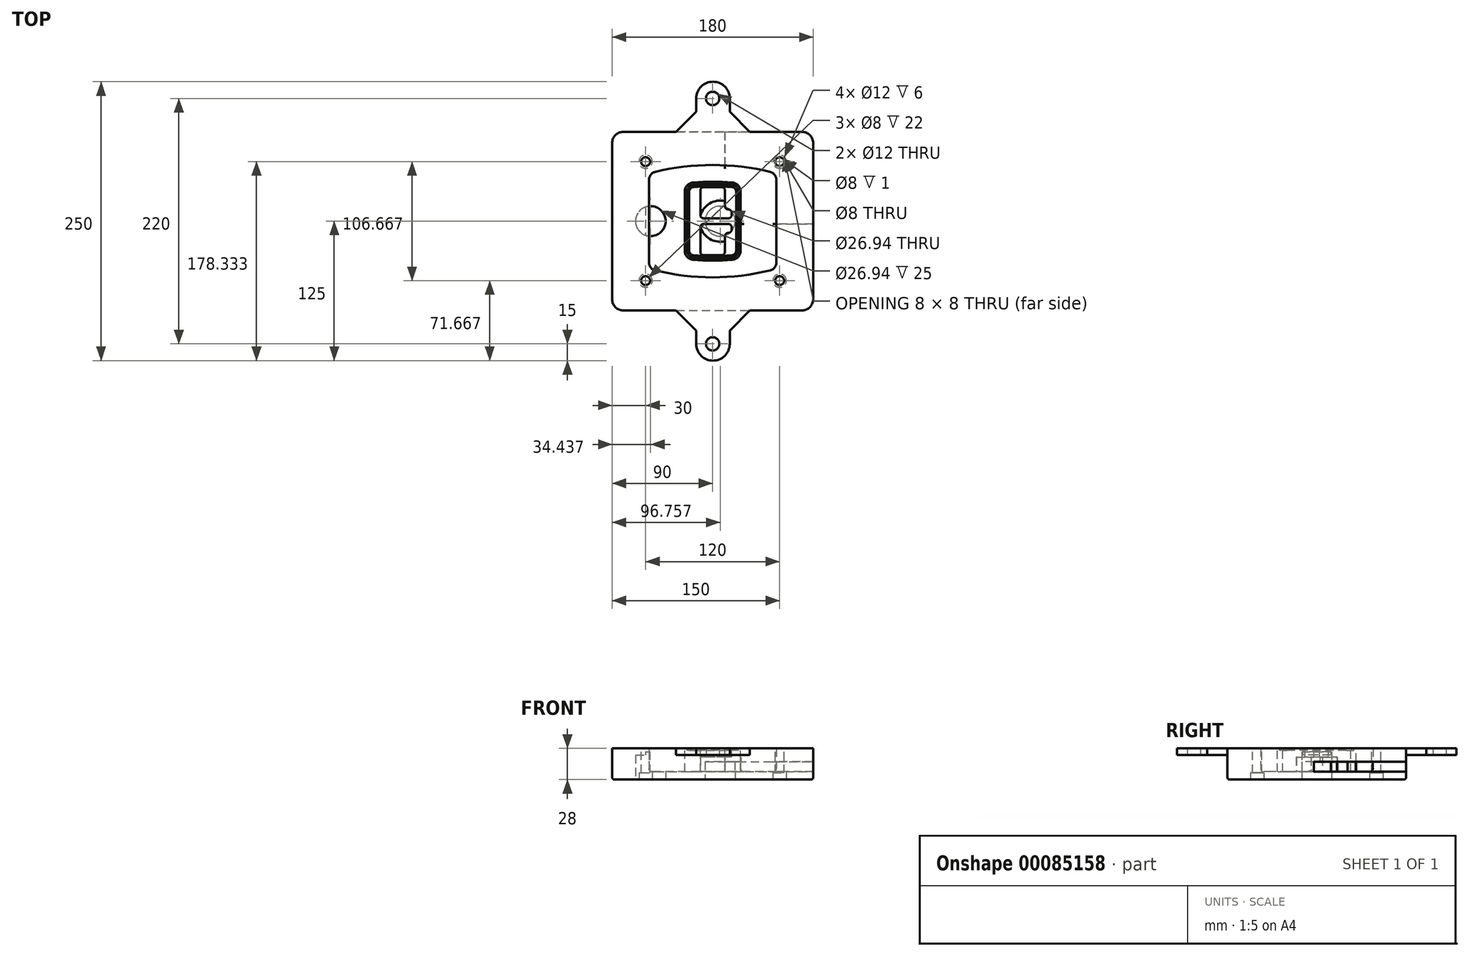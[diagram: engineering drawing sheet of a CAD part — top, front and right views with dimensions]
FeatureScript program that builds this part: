
annotation { "Feature Type Name" : "Feature", "Feature Type Description" : "" }
export const myFeature = defineFeature(function(context is Context, id is Id, definition is map)
    precondition{}
    {
        {
            var Q0;
            Q0=qCreatedBy(makeId("Top.planeOp"),FACE);
            var sketch = newSketch(context, id + "F0", { "sketchPlane" : qUnion([Q0])});
            skPoint(sketch, "E0.rect.middle", {"position": v(0, 0) * mm});
            skLineSegment(sketch, "E1.bottom", {"start": v(-80, -80) * mm, "end": v(80, -80) * mm});
            skLineSegment(sketch, "E1.top", {"start": v(-80, 80) * mm, "end": v(80, 80) * mm});
            skLineSegment(sketch, "E1.left", {"start": v(-90, -70) * mm, "end": v(-90, 70) * mm});
            skLineSegment(sketch, "E1.right", {"start": v(90, -70) * mm, "end": v(90, 70) * mm});
            skLineSegment(sketch, "E2", {"start": v(-90, 80) * mm, "end": v(90, -80) * mm, "construction": true});
            skLineSegment(sketch, "E3", {"start": v(90, 80) * mm, "end": v(-90, -80) * mm, "construction": true});
            skCircle(sketch, "E4", {"center": v(-60, 53.33) * mm, "radius": 4 * mm});
            skCircle(sketch, "E5", {"center": v(60, 53.33) * mm, "radius": 4 * mm});
            skCircle(sketch, "E6", {"center": v(60, -53.33) * mm, "radius": 4 * mm});
            skCircle(sketch, "E7", {"center": v(-60, -53.33) * mm, "radius": 4 * mm});
            skLineSegment(sketch, "E8", {"start": v(-60, 53.33) * mm, "end": v(60, 53.33) * mm, "construction": true});
            skLineSegment(sketch, "E9", {"start": v(60, 53.33) * mm, "end": v(60, -53.33) * mm, "construction": true});
            skLineSegment(sketch, "E10", {"start": v(60, -53.33) * mm, "end": v(-60, -53.33) * mm, "construction": true});
            skLineSegment(sketch, "E11", {"start": v(-60, -53.33) * mm, "end": v(-60, 53.33) * mm, "construction": true});
            skLineSegment(sketch, "E12", {"start": v(-60, 37.3) * mm, "end": v(-60, -37.3) * mm});
            skLineSegment(sketch, "E13", {"start": v(60, 37.3) * mm, "end": v(60, -37.3) * mm});
            skArc(sketch, "E14", {"start": v(52.38, 47.01) * mm, "mid": v(0, 53.33) * mm, "end": v(-52.38, 47.01) * mm});
            skArc(sketch, "E15", {"start": v(-52.38, -47.01) * mm, "mid": v(0, -53.33) * mm, "end": v(52.38, -47.01) * mm});
            skLineSegment(sketch, "E16", {"start": v(-60, 0) * mm, "end": v(60, 0) * mm, "construction": true});
            skPoint(sketch, "E17.visualSharp", {"position": v(-60, -45) * mm});
            skArc(sketch, "E17.filletArc", {"start": v(-60, -37.3) * mm, "mid": v(-57.87, -43.47) * mm, "end": v(-52.38, -47.01) * mm});
            skPoint(sketch, "E18.visualSharp", {"position": v(-60, 45) * mm});
            skArc(sketch, "E18.filletArc", {"start": v(-52.38, 47.01) * mm, "mid": v(-57.87, 43.47) * mm, "end": v(-60, 37.3) * mm});
            skPoint(sketch, "E19.visualSharp", {"position": v(60, 45) * mm});
            skArc(sketch, "E19.filletArc", {"start": v(60, 37.3) * mm, "mid": v(57.87, 43.47) * mm, "end": v(52.38, 47.01) * mm});
            skPoint(sketch, "E20.visualSharp", {"position": v(60, -45) * mm});
            skArc(sketch, "E20.filletArc", {"start": v(52.38, -47.01) * mm, "mid": v(57.87, -43.47) * mm, "end": v(60, -37.3) * mm});
            skPoint(sketch, "E21.visualSharp", {"position": v(-90, 80) * mm});
            skArc(sketch, "E21.filletArc", {"start": v(-80, 80) * mm, "mid": v(-87.07, 77.07) * mm, "end": v(-90, 70) * mm});
            skPoint(sketch, "E22.visualSharp", {"position": v(90, 80) * mm});
            skArc(sketch, "E22.filletArc", {"start": v(90, 70) * mm, "mid": v(87.07, 77.07) * mm, "end": v(80, 80) * mm});
            skPoint(sketch, "E23.visualSharp", {"position": v(90, -80) * mm});
            skArc(sketch, "E23.filletArc", {"start": v(80, -80) * mm, "mid": v(87.07, -77.07) * mm, "end": v(90, -70) * mm});
            skPoint(sketch, "E24.visualSharp", {"position": v(-90, -80) * mm});
            skArc(sketch, "E24.filletArc", {"start": v(-90, -70) * mm, "mid": v(-87.07, -77.07) * mm, "end": v(-80, -80) * mm});
            skArc(sketch, "E25.0", {"start": v(57, 37.3) * mm, "mid": v(55.5, 41.62) * mm, "end": v(51.67, 44.1) * mm});
            skLineSegment(sketch, "E25.1", {"start": v(57, 37.3) * mm, "end": v(57, -37.3) * mm});
            skArc(sketch, "E25.2", {"start": v(51.67, -44.1) * mm, "mid": v(55.5, -41.62) * mm, "end": v(57, -37.3) * mm});
            skArc(sketch, "E25.3", {"start": v(-51.67, -44.1) * mm, "mid": v(0, -50.33) * mm, "end": v(51.67, -44.1) * mm});
            skArc(sketch, "E25.4", {"start": v(-57, -37.3) * mm, "mid": v(-55.5, -41.62) * mm, "end": v(-51.67, -44.1) * mm});
            skArc(sketch, "E25.5", {"start": v(51.67, 44.1) * mm, "mid": v(0, 50.33) * mm, "end": v(-51.67, 44.1) * mm});
            skLineSegment(sketch, "E25.6", {"start": v(-57, 37.3) * mm, "end": v(-57, -37.3) * mm});
            skArc(sketch, "E25.7", {"start": v(-51.67, 44.1) * mm, "mid": v(-55.5, 41.62) * mm, "end": v(-57, 37.3) * mm});
            skArc(sketch, "E26.0", {"start": v(-53.33, 50.9) * mm, "mid": v(-61.01, 45.94) * mm, "end": v(-64, 37.3) * mm});
            skArc(sketch, "E26.1", {"start": v(53.33, 50.9) * mm, "mid": v(0, 57.33) * mm, "end": v(-53.33, 50.9) * mm});
            skArc(sketch, "E26.2", {"start": v(64, 37.3) * mm, "mid": v(61.01, 45.94) * mm, "end": v(53.33, 50.9) * mm});
            skLineSegment(sketch, "E26.3", {"start": v(64, 37.3) * mm, "end": v(64, -37.3) * mm});
            skArc(sketch, "E26.4", {"start": v(53.33, -50.9) * mm, "mid": v(61.01, -45.94) * mm, "end": v(64, -37.3) * mm});
            skLineSegment(sketch, "E26.5", {"start": v(-64, 37.3) * mm, "end": v(-64, -37.3) * mm});
            skArc(sketch, "E26.6", {"start": v(-53.33, -50.9) * mm, "mid": v(0, -57.33) * mm, "end": v(53.33, -50.9) * mm});
            skArc(sketch, "E26.7", {"start": v(-64, -37.3) * mm, "mid": v(-61.01, -45.94) * mm, "end": v(-53.33, -50.9) * mm});
            skSolve(sketch);
        }
        {
            var Q0;
            Q0=makeQuery(id+"F0.imprint","IMPRINT",FACE,{"disambiguationData":[TD([[makeQuery(id+"F0.imprint","IMPRINT",EDGE,{"derivedFrom":sQuery(id+"F0.wireOp",EDGE,"E1.bottom")}),1.0]])]});
            var Q1;
            Q1=makeQuery(id+"F0.imprint","IMPRINT",FACE,{"disambiguationData":[TD([[makeQuery(id+"F0.imprint","IMPRINT",EDGE,{"derivedFrom":sQuery(id+"F0.wireOp",EDGE,"E12")}),1.0]])]});
            var Q2;
            Q2=makeQuery(id+"F0.imprint","IMPRINT",FACE,{"disambiguationData":[TD([[makeQuery(id+"F0.imprint","IMPRINT",EDGE,{"derivedFrom":sQuery(id+"F0.wireOp",EDGE,"E25.0")}),1.0]])]});
            var Q3;
            Q3=makeQuery(id+"F0.imprint","IMPRINT",FACE,{"disambiguationData":[TD([[makeQuery(id+"F0.imprint","IMPRINT",EDGE,{"derivedFrom":sQuery(id+"F0.wireOp",EDGE,"E12")}),-1.0]])]});
            extrude(context, id + "F1", {"entities" : qUnion([Q0, Q1, Q2, Q3]), "oppositeDirection" : true, "depth" : 25 * mm});
        }
        {
            var Q0;
            Q0=makeQuery(id+"F0.imprint","IMPRINT",FACE,{"disambiguationData":[TD([[makeQuery(id+"F0.imprint","IMPRINT",EDGE,{"derivedFrom":sQuery(id+"F0.wireOp",EDGE,"E12")}),1.0]])]});
            extrude(context, id + "F2", {"entities" : qUnion([Q0]), "operationType" : NewBodyOperationType.ADD, "depth" : 3 * mm});
        }
        {
            var Q0;
            Q0=makeQuery(id+"F0.imprint","IMPRINT",FACE,{"disambiguationData":[TD([[makeQuery(id+"F0.imprint","IMPRINT",EDGE,{"derivedFrom":sQuery(id+"F0.wireOp",EDGE,"E25.0")}),1.0]])]});
            extrude(context, id + "F3", {"entities" : qUnion([Q0]), "operationType" : NewBodyOperationType.REMOVE, "oppositeDirection" : true, "depth" : 18 * mm});
        }
        {
            var Q0;
            Q0=makeQuery(id+"F2.opExtrude","CAP_FACE",FACE,{"disambiguationData":[OSD([sQuery(id+"F0.wireOp",EDGE,"E12"),sQuery(id+"F0.wireOp",EDGE,"E13"),sQuery(id+"F0.wireOp",EDGE,"E14"),sQuery(id+"F0.wireOp",EDGE,"E15"),sQuery(id+"F0.wireOp",EDGE,"E17.filletArc"),sQuery(id+"F0.wireOp",EDGE,"E18.filletArc"),sQuery(id+"F0.wireOp",EDGE,"E19.filletArc"),sQuery(id+"F0.wireOp",EDGE,"E20.filletArc"),sQuery(id+"F0.wireOp",EDGE,"E25.0"),sQuery(id+"F0.wireOp",EDGE,"E25.1"),sQuery(id+"F0.wireOp",EDGE,"E25.2"),sQuery(id+"F0.wireOp",EDGE,"E25.3"),sQuery(id+"F0.wireOp",EDGE,"E25.4"),sQuery(id+"F0.wireOp",EDGE,"E25.5"),sQuery(id+"F0.wireOp",EDGE,"E25.6"),sQuery(id+"F0.wireOp",EDGE,"E25.7")])],"isStart":false});
            var sketch = newSketch(context, id + "F4", { "sketchPlane" : qUnion([Q0])});
            skArc(sketch, "E27.0", {"start": v(-17.7, -34.56) * mm, "mid": v(0, -35.33) * mm, "end": v(17.7, -34.56) * mm});
            skArc(sketch, "E28.0", {"start": v(17.7, 34.56) * mm, "mid": v(0, 35.33) * mm, "end": v(-17.7, 34.56) * mm});
            skLineSegment(sketch, "E29", {"start": v(-25, 26.59) * mm, "end": v(-25, -26.59) * mm});
            skLineSegment(sketch, "E30", {"start": v(25, 26.59) * mm, "end": v(25, -26.59) * mm});
            skLineSegment(sketch, "E31", {"start": v(-25, 33.78) * mm, "end": v(25, 33.78) * mm, "construction": true});
            skLineSegment(sketch, "E32", {"start": v(-25, -33.78) * mm, "end": v(25, -33.78) * mm, "construction": true});
            skPoint(sketch, "E33.visualSharp", {"position": v(-25, 33.78) * mm});
            skArc(sketch, "E33.filletArc", {"start": v(-17.7, 34.56) * mm, "mid": v(-22.9, 32) * mm, "end": v(-25, 26.59) * mm});
            skPoint(sketch, "E34.visualSharp", {"position": v(25, 33.78) * mm});
            skArc(sketch, "E34.filletArc", {"start": v(25, 26.59) * mm, "mid": v(22.9, 32) * mm, "end": v(17.7, 34.56) * mm});
            skPoint(sketch, "E35.visualSharp", {"position": v(25, -33.78) * mm});
            skArc(sketch, "E35.filletArc", {"start": v(17.7, -34.56) * mm, "mid": v(22.9, -32) * mm, "end": v(25, -26.59) * mm});
            skPoint(sketch, "E36.visualSharp", {"position": v(-25, -33.78) * mm});
            skArc(sketch, "E36.filletArc", {"start": v(-25, -26.59) * mm, "mid": v(-22.9, -32) * mm, "end": v(-17.7, -34.56) * mm});
            skArc(sketch, "E37.0", {"start": v(51.67, 44.1) * mm, "mid": v(0, 50.33) * mm, "end": v(-51.67, 44.1) * mm});
            skArc(sketch, "E37.1", {"start": v(-51.67, 44.1) * mm, "mid": v(-55.5, 41.62) * mm, "end": v(-57, 37.3) * mm});
            skLineSegment(sketch, "E37.2", {"start": v(-57, 37.3) * mm, "end": v(-57, -37.3) * mm});
            skArc(sketch, "E37.3", {"start": v(-57, -37.3) * mm, "mid": v(-55.5, -41.62) * mm, "end": v(-51.67, -44.1) * mm});
            skArc(sketch, "E37.4", {"start": v(-51.67, -44.1) * mm, "mid": v(0, -50.33) * mm, "end": v(51.67, -44.1) * mm});
            skArc(sketch, "E37.5", {"start": v(51.67, -44.1) * mm, "mid": v(55.5, -41.62) * mm, "end": v(57, -37.3) * mm});
            skLineSegment(sketch, "E37.6", {"start": v(57, 37.3) * mm, "end": v(57, -37.3) * mm});
            skArc(sketch, "E37.7", {"start": v(57, 37.3) * mm, "mid": v(55.5, 41.62) * mm, "end": v(51.67, 44.1) * mm});
            skLineSegment(sketch, "E38.0", {"start": v(23, 26.59) * mm, "end": v(23, -26.59) * mm});
            skArc(sketch, "E38.1", {"start": v(17.53, -32.56) * mm, "mid": v(21.42, -30.64) * mm, "end": v(23, -26.59) * mm});
            skArc(sketch, "E38.2", {"start": v(-17.53, -32.56) * mm, "mid": v(0, -33.33) * mm, "end": v(17.53, -32.56) * mm});
            skArc(sketch, "E38.3", {"start": v(-23, -26.59) * mm, "mid": v(-21.42, -30.64) * mm, "end": v(-17.53, -32.56) * mm});
            skLineSegment(sketch, "E38.4", {"start": v(-23, 26.59) * mm, "end": v(-23, -26.59) * mm});
            skArc(sketch, "E38.5", {"start": v(23, 26.59) * mm, "mid": v(21.42, 30.64) * mm, "end": v(17.53, 32.56) * mm});
            skArc(sketch, "E38.6", {"start": v(-17.53, 32.56) * mm, "mid": v(-21.42, 30.64) * mm, "end": v(-23, 26.59) * mm});
            skArc(sketch, "E38.7", {"start": v(17.53, 32.56) * mm, "mid": v(0, 33.33) * mm, "end": v(-17.53, 32.56) * mm});
            skArc(sketch, "E39.0", {"start": v(21, 26.59) * mm, "mid": v(19.95, 29.29) * mm, "end": v(17.35, 30.57) * mm});
            skLineSegment(sketch, "E39.1", {"start": v(21, 26.59) * mm, "end": v(21, -26.59) * mm});
            skArc(sketch, "E39.2", {"start": v(17.35, -30.57) * mm, "mid": v(19.95, -29.29) * mm, "end": v(21, -26.59) * mm});
            skArc(sketch, "E39.3", {"start": v(-17.35, -30.57) * mm, "mid": v(0, -31.33) * mm, "end": v(17.35, -30.57) * mm});
            skArc(sketch, "E39.4", {"start": v(-21, -26.59) * mm, "mid": v(-19.95, -29.29) * mm, "end": v(-17.35, -30.57) * mm});
            skArc(sketch, "E39.5", {"start": v(17.35, 30.57) * mm, "mid": v(0, 31.33) * mm, "end": v(-17.35, 30.57) * mm});
            skLineSegment(sketch, "E39.6", {"start": v(-21, 26.59) * mm, "end": v(-21, -26.59) * mm});
            skArc(sketch, "E39.7", {"start": v(-17.35, 30.57) * mm, "mid": v(-19.95, 29.29) * mm, "end": v(-21, 26.59) * mm});
            skLineSegment(sketch, "E40", {"start": v(-25, 0) * mm, "end": v(25, 0) * mm, "construction": true});
            skLineSegment(sketch, "E41", {"start": v(-11, 5.5) * mm, "end": v(-11, 27.5) * mm});
            skLineSegment(sketch, "E42", {"start": v(-8, 30.5) * mm, "end": v(8, 30.5) * mm});
            skLineSegment(sketch, "E43", {"start": v(11, 27.5) * mm, "end": v(11, 13.5) * mm});
            skLineSegment(sketch, "E44", {"start": v(14, 10.5) * mm, "end": v(14, 10.5) * mm});
            skLineSegment(sketch, "E45", {"start": v(17, 7.5) * mm, "end": v(17, 5.5) * mm});
            skLineSegment(sketch, "E46", {"start": v(14, 2.5) * mm, "end": v(-8, 2.5) * mm});
            skPoint(sketch, "E47.visualSharp", {"position": v(-11, 30.5) * mm});
            skArc(sketch, "E47.filletArc", {"start": v(-8, 30.5) * mm, "mid": v(-10.12, 29.62) * mm, "end": v(-11, 27.5) * mm});
            skPoint(sketch, "E48.visualSharp", {"position": v(11, 30.5) * mm});
            skArc(sketch, "E48.filletArc", {"start": v(11, 27.5) * mm, "mid": v(10.12, 29.62) * mm, "end": v(8, 30.5) * mm});
            skPoint(sketch, "E49.visualSharp", {"position": v(11, 10.5) * mm});
            skArc(sketch, "E49.filletArc", {"start": v(11, 13.5) * mm, "mid": v(11.88, 11.38) * mm, "end": v(14, 10.5) * mm});
            skPoint(sketch, "E50.visualSharp", {"position": v(17, 10.5) * mm});
            skArc(sketch, "E50.filletArc", {"start": v(17, 7.5) * mm, "mid": v(16.12, 9.62) * mm, "end": v(14, 10.5) * mm});
            skPoint(sketch, "E51.visualSharp", {"position": v(17, 2.5) * mm});
            skArc(sketch, "E51.filletArc", {"start": v(14, 2.5) * mm, "mid": v(16.12, 3.38) * mm, "end": v(17, 5.5) * mm});
            skPoint(sketch, "E52.visualSharp", {"position": v(-11, 2.5) * mm});
            skArc(sketch, "E52.filletArc", {"start": v(-11, 5.5) * mm, "mid": v(-10.12, 3.38) * mm, "end": v(-8, 2.5) * mm});
            skLineSegment(sketch, "E53.0.MirrorCS", {"start": v(14, -2.5) * mm, "end": v(-8, -2.5) * mm});
            skArc(sketch, "E54.0.MirrorCS", {"start": v(-11, -5.5) * mm, "mid": v(-10.12, -3.38) * mm, "end": v(-8, -2.5) * mm});
            skLineSegment(sketch, "E55.0.MirrorCS", {"start": v(-11, -5.5) * mm, "end": v(-11, -27.5) * mm});
            skArc(sketch, "E56.0.MirrorCS", {"start": v(-8, -30.5) * mm, "mid": v(-10.12, -29.62) * mm, "end": v(-11, -27.5) * mm});
            skLineSegment(sketch, "E57.0.MirrorCS", {"start": v(-8, -30.5) * mm, "end": v(8, -30.5) * mm});
            skArc(sketch, "E58.0.MirrorCS", {"start": v(11, -27.5) * mm, "mid": v(10.12, -29.62) * mm, "end": v(8, -30.5) * mm});
            skLineSegment(sketch, "E59.0.MirrorCS", {"start": v(11, -27.5) * mm, "end": v(11, -13.5) * mm});
            skArc(sketch, "E60.0.MirrorCS", {"start": v(11, -13.5) * mm, "mid": v(11.88, -11.38) * mm, "end": v(14, -10.5) * mm});
            skArc(sketch, "E61.0.MirrorCS", {"start": v(17, -7.5) * mm, "mid": v(16.12, -9.62) * mm, "end": v(14, -10.5) * mm});
            skLineSegment(sketch, "E62.0.MirrorCS", {"start": v(17, -7.5) * mm, "end": v(17, -5.5) * mm});
            skArc(sketch, "E63.0.MirrorCS", {"start": v(14, -2.5) * mm, "mid": v(16.12, -3.38) * mm, "end": v(17, -5.5) * mm});
            skSolve(sketch);
        }
        {
            var Q0;
            Q0=makeQuery(id+"F4.imprint","IMPRINT",FACE,{"disambiguationData":[TD([[makeQuery(id+"F4.imprint","IMPRINT",EDGE,{"derivedFrom":sQuery(id+"F4.wireOp",EDGE,"E27.0")}),1.0]])]});
            var Q1;
            Q1=makeQuery(id+"F4.imprint","IMPRINT",FACE,{"disambiguationData":[TD([[makeQuery(id+"F4.imprint","IMPRINT",EDGE,{"derivedFrom":sQuery(id+"F4.wireOp",EDGE,"E38.0")}),-1.0]])]});
            var Q2;
            Q2=makeQuery(id+"F4.imprint","IMPRINT",FACE,{"disambiguationData":[TD([[makeQuery(id+"F4.imprint","IMPRINT",EDGE,{"derivedFrom":sQuery(id+"F4.wireOp",EDGE,"E39.0")}),1.0]])]});
            extrude(context, id + "F5", {"entities" : qUnion([Q0, Q1, Q2]), "operationType" : NewBodyOperationType.ADD, "endBound" : BoundingType.UP_TO_NEXT, "oppositeDirection" : true, "depth" : 25 * mm});
        }
        {
            var Q0;
            Q0=makeQuery(id+"F4.imprint","IMPRINT",FACE,{"disambiguationData":[TD([[makeQuery(id+"F4.imprint","IMPRINT",EDGE,{"derivedFrom":sQuery(id+"F4.wireOp",EDGE,"E38.0")}),-1.0]])]});
            extrude(context, id + "F6", {"entities" : qUnion([Q0]), "operationType" : NewBodyOperationType.REMOVE, "oppositeDirection" : true, "depth" : 2 * mm});
        }
        {
            var Q0;
            Q0=makeQuery(id+"F1.opExtrude","CAP_FACE",FACE,{"disambiguationData":[OSD([sQuery(id+"F0.wireOp",EDGE,"E1.bottom"),sQuery(id+"F0.wireOp",EDGE,"E1.top"),sQuery(id+"F0.wireOp",EDGE,"E1.left"),sQuery(id+"F0.wireOp",EDGE,"E1.right"),sQuery(id+"F0.wireOp",EDGE,"E4"),sQuery(id+"F0.wireOp",EDGE,"E5"),sQuery(id+"F0.wireOp",EDGE,"E6"),sQuery(id+"F0.wireOp",EDGE,"E7"),sQuery(id+"F0.wireOp",EDGE,"E21.filletArc"),sQuery(id+"F0.wireOp",EDGE,"E22.filletArc"),sQuery(id+"F0.wireOp",EDGE,"E23.filletArc"),sQuery(id+"F0.wireOp",EDGE,"E24.filletArc")])],"isStart":false});
            var sketch = newSketch(context, id + "F7", { "sketchPlane" : qUnion([Q0])});
            skCircle(sketch, "E64", {"center": v(6.76, 0) * mm, "radius": 13.47 * mm});
            skCircle(sketch, "E65", {"center": v(-55.56, 0) * mm, "radius": 13.47 * mm});
            skLineSegment(sketch, "E66", {"start": v(90, 0) * mm, "end": v(-90, 0) * mm});
            skCircle(sketch, "E67", {"center": v(6.76, 0) * mm, "radius": 18.47 * mm});
            skCircle(sketch, "E68", {"center": v(60, -53.33) * mm, "radius": 6 * mm});
            skCircle(sketch, "E69", {"center": v(-60, -53.33) * mm, "radius": 6 * mm});
            skCircle(sketch, "E70", {"center": v(-60, 53.33) * mm, "radius": 6 * mm});
            skCircle(sketch, "E71", {"center": v(60, 53.33) * mm, "radius": 6 * mm});
            skSolve(sketch);
        }
        {
            var Q0;
            {var subQ1=sQuery(id+"F7.wireOp",EDGE,"E66");var subQ4=sQuery(id+"F7.wireOp",EDGE,"E64");var subQ6=makeQuery(id+"F7.imprint","INTERSECT",VERTEX,{"disambiguationData":[OD(0.0)],"derivedFrom":[subQ4,subQ1]});Q0=makeQuery(id+"F7.imprint","IMPRINT",FACE,{"disambiguationData":[TD([[makeQuery(id+"F7.imprint","IMPRINT",EDGE,{"disambiguationData":[TD([[subQ6,-1.0]])],"derivedFrom":subQ4}),-1.0]])]});}
            var Q1;
            {var subQ0=sQuery(id+"F7.wireOp",EDGE,"E66");var subQ1=sQuery(id+"F7.wireOp",EDGE,"E64");var subQ3=makeQuery(id+"F7.imprint","INTERSECT",VERTEX,{"disambiguationData":[OD(0.0)],"derivedFrom":[subQ1,subQ0]});Q1=makeQuery(id+"F7.imprint","IMPRINT",FACE,{"disambiguationData":[TD([[makeQuery(id+"F7.imprint","IMPRINT",EDGE,{"disambiguationData":[TD([[subQ3,-1.0]])],"derivedFrom":subQ1}),1.0]])]});}
            var Q2;
            {var subQ0=sQuery(id+"F7.wireOp",EDGE,"E66");var subQ1=sQuery(id+"F7.wireOp",EDGE,"E64");var subQ3=makeQuery(id+"F7.imprint","INTERSECT",VERTEX,{"disambiguationData":[OD(0.0)],"derivedFrom":[subQ1,subQ0]});Q2=makeQuery(id+"F7.imprint","IMPRINT",FACE,{"disambiguationData":[TD([[makeQuery(id+"F7.imprint","IMPRINT",EDGE,{"disambiguationData":[TD([[subQ3,1.0]])],"derivedFrom":subQ1}),1.0]])]});}
            var Q3;
            {var subQ1=sQuery(id+"F7.wireOp",EDGE,"E66");var subQ4=sQuery(id+"F7.wireOp",EDGE,"E64");var subQ6=makeQuery(id+"F7.imprint","INTERSECT",VERTEX,{"disambiguationData":[OD(0.0)],"derivedFrom":[subQ4,subQ1]});Q3=makeQuery(id+"F7.imprint","IMPRINT",FACE,{"disambiguationData":[TD([[makeQuery(id+"F7.imprint","IMPRINT",EDGE,{"disambiguationData":[TD([[subQ6,1.0]])],"derivedFrom":subQ4}),-1.0]])]});}
            extrude(context, id + "F8", {"entities" : qUnion([Q0, Q1, Q2, Q3]), "operationType" : NewBodyOperationType.ADD, "oppositeDirection" : true, "depth" : 20 * mm});
        }
        {
            var Q0;
            {var subQ0=sQuery(id+"F7.wireOp",EDGE,"E66");var subQ1=sQuery(id+"F7.wireOp",EDGE,"E64");var subQ3=makeQuery(id+"F7.imprint","INTERSECT",VERTEX,{"disambiguationData":[OD(0.0)],"derivedFrom":[subQ1,subQ0]});Q0=makeQuery(id+"F7.imprint","IMPRINT",FACE,{"disambiguationData":[TD([[makeQuery(id+"F7.imprint","IMPRINT",EDGE,{"disambiguationData":[TD([[subQ3,-1.0]])],"derivedFrom":subQ1}),1.0]])]});}
            var Q1;
            {var subQ0=sQuery(id+"F7.wireOp",EDGE,"E66");var subQ1=sQuery(id+"F7.wireOp",EDGE,"E64");var subQ3=makeQuery(id+"F7.imprint","INTERSECT",VERTEX,{"disambiguationData":[OD(0.0)],"derivedFrom":[subQ1,subQ0]});Q1=makeQuery(id+"F7.imprint","IMPRINT",FACE,{"disambiguationData":[TD([[makeQuery(id+"F7.imprint","IMPRINT",EDGE,{"disambiguationData":[TD([[subQ3,1.0]])],"derivedFrom":subQ1}),1.0]])]});}
            extrude(context, id + "F9", {"entities" : qUnion([Q0, Q1]), "operationType" : NewBodyOperationType.REMOVE, "oppositeDirection" : true, "depth" : 16 * mm});
        }
        {
            var Q0;
            {var subQ0=sQuery(id+"F7.wireOp",EDGE,"E66");var subQ1=sQuery(id+"F7.wireOp",EDGE,"E65");var subQ3=makeQuery(id+"F7.imprint","INTERSECT",VERTEX,{"disambiguationData":[OD(0.0)],"derivedFrom":[subQ1,subQ0]});Q0=makeQuery(id+"F7.imprint","IMPRINT",FACE,{"disambiguationData":[TD([[makeQuery(id+"F7.imprint","IMPRINT",EDGE,{"disambiguationData":[TD([[subQ3,-1.0]])],"derivedFrom":subQ1}),1.0]])]});}
            var Q1;
            {var subQ0=sQuery(id+"F7.wireOp",EDGE,"E66");var subQ1=sQuery(id+"F7.wireOp",EDGE,"E65");var subQ3=makeQuery(id+"F7.imprint","INTERSECT",VERTEX,{"disambiguationData":[OD(0.0)],"derivedFrom":[subQ1,subQ0]});Q1=makeQuery(id+"F7.imprint","IMPRINT",FACE,{"disambiguationData":[TD([[makeQuery(id+"F7.imprint","IMPRINT",EDGE,{"disambiguationData":[TD([[subQ3,1.0]])],"derivedFrom":subQ1}),1.0]])]});}
            extrude(context, id + "F10", {"entities" : qUnion([Q0, Q1]), "operationType" : NewBodyOperationType.REMOVE, "oppositeDirection" : true, "depth" : 25 * mm});
        }
        {
            var Q0;
            Q0=makeQuery(id+"F7.imprint","IMPRINT",FACE,{"disambiguationData":[TD([[makeQuery(id+"F7.imprint","IMPRINT",EDGE,{"derivedFrom":sQuery(id+"F7.wireOp",EDGE,"E68")}),1.0]])]});
            var Q1;
            Q1=makeQuery(id+"F7.imprint","IMPRINT",FACE,{"disambiguationData":[TD([[makeQuery(id+"F7.imprint","IMPRINT",EDGE,{"derivedFrom":makeQuery(id+"F1.opExtrude","CAP_EDGE",EDGE,{"disambiguationData":[OSD([sQuery(id+"F0.wireOp",EDGE,"E5")])],"isStart":false})}),-1.0]])]});
            var Q2;
            Q2=makeQuery(id+"F7.imprint","IMPRINT",FACE,{"disambiguationData":[TD([[makeQuery(id+"F7.imprint","IMPRINT",EDGE,{"derivedFrom":sQuery(id+"F7.wireOp",EDGE,"E69")}),1.0]])]});
            var Q3;
            Q3=makeQuery(id+"F7.imprint","IMPRINT",FACE,{"disambiguationData":[TD([[makeQuery(id+"F7.imprint","IMPRINT",EDGE,{"derivedFrom":makeQuery(id+"F1.opExtrude","CAP_EDGE",EDGE,{"disambiguationData":[OSD([sQuery(id+"F0.wireOp",EDGE,"E4")])],"isStart":false})}),-1.0]])]});
            var Q4;
            Q4=makeQuery(id+"F7.imprint","IMPRINT",FACE,{"disambiguationData":[TD([[makeQuery(id+"F7.imprint","IMPRINT",EDGE,{"derivedFrom":sQuery(id+"F7.wireOp",EDGE,"E70")}),1.0]])]});
            var Q5;
            Q5=makeQuery(id+"F7.imprint","IMPRINT",FACE,{"disambiguationData":[TD([[makeQuery(id+"F7.imprint","IMPRINT",EDGE,{"derivedFrom":makeQuery(id+"F1.opExtrude","CAP_EDGE",EDGE,{"disambiguationData":[OSD([sQuery(id+"F0.wireOp",EDGE,"E7")])],"isStart":false})}),-1.0]])]});
            var Q6;
            Q6=makeQuery(id+"F7.imprint","IMPRINT",FACE,{"disambiguationData":[TD([[makeQuery(id+"F7.imprint","IMPRINT",EDGE,{"derivedFrom":sQuery(id+"F7.wireOp",EDGE,"E71")}),1.0]])]});
            var Q7;
            Q7=makeQuery(id+"F7.imprint","IMPRINT",FACE,{"disambiguationData":[TD([[makeQuery(id+"F7.imprint","IMPRINT",EDGE,{"derivedFrom":makeQuery(id+"F1.opExtrude","CAP_EDGE",EDGE,{"disambiguationData":[OSD([sQuery(id+"F0.wireOp",EDGE,"E6")])],"isStart":false})}),-1.0]])]});
            extrude(context, id + "F11", {"entities" : qUnion([Q0, Q1, Q2, Q3, Q4, Q5, Q6, Q7]), "operationType" : NewBodyOperationType.REMOVE, "oppositeDirection" : true, "depth" : 6 * mm});
        }
        {
            var Q0;
            Q0=makeQuery(id+"F9.boolean.opBoolean","COPY",FACE,{"derivedFrom":makeQuery(id+"F9.opExtrude","CAP_FACE",FACE,{"disambiguationData":[OSD([sQuery(id+"F7.wireOp",EDGE,"E64")])],"isStart":false})});
            var sketch = newSketch(context, id + "F12", { "sketchPlane" : qUnion([Q0])});
            skArc(sketch, "E72.0", {"start": v(11, -88.19) * mm, "mid": v(97.1, -83.6) * mm, "end": v(92.5, 2.5) * mm});
            skLineSegment(sketch, "E72.1", {"start": v(11, -17.97) * mm, "end": v(11, -17.97) * mm});
            skLineSegment(sketch, "E73", {"start": v(92.5, -105.13) * mm, "end": v(102.3, -105.13) * mm});
            skLineSegment(sketch, "E74.0", {"start": v(92.5, 2.5) * mm, "end": v(14, 2.5) * mm});
            skArc(sketch, "E74.1", {"start": v(14, 2.5) * mm, "mid": v(16.12, 3.38) * mm, "end": v(17, 5.5) * mm});
            skLineSegment(sketch, "E74.2", {"start": v(17, 7.5) * mm, "end": v(17, 5.5) * mm});
            skArc(sketch, "E74.3", {"start": v(17, 7.5) * mm, "mid": v(16.12, 9.62) * mm, "end": v(14, 10.5) * mm});
            skArc(sketch, "E74.4", {"start": v(11, 13.5) * mm, "mid": v(11.88, 11.38) * mm, "end": v(14, 10.5) * mm});
            skLineSegment(sketch, "E74.5", {"start": v(11, 13.5) * mm, "end": v(11, -88.19) * mm});
            skLineSegment(sketch, "E74.7", {"start": v(92.5, -2.5) * mm, "end": v(14, -2.5) * mm});
            skArc(sketch, "E74.8", {"start": v(14, -2.5) * mm, "mid": v(16.12, -3.38) * mm, "end": v(17, -5.5) * mm});
            skLineSegment(sketch, "E74.9", {"start": v(17, -7.5) * mm, "end": v(17, -5.5) * mm});
            skArc(sketch, "E74.10", {"start": v(17, -7.5) * mm, "mid": v(16.12, -9.62) * mm, "end": v(14, -10.5) * mm});
            skArc(sketch, "E74.11", {"start": v(11, -13.5) * mm, "mid": v(11.88, -11.38) * mm, "end": v(14, -10.5) * mm});
            skLineSegment(sketch, "E74.12", {"start": v(11, -17.97) * mm, "end": v(11, -13.5) * mm});
            skPoint(sketch, "E75.orphan", {"position": v(11, -27.5) * mm});
            skPoint(sketch, "E76.orphan", {"position": v(-8, -2.5) * mm});
            skPoint(sketch, "E77.orphan", {"position": v(-8, 2.5) * mm});
            skPoint(sketch, "E78.orphan", {"position": v(11, 27.5) * mm});
            skSolve(sketch);
        }
        {
            var Q0;
            {var subQ7=sQuery(id+"F12.wireOp",EDGE,"E72.0");var subQ14=sQuery(id+"F12.wireOp",EDGE,"E72.1");var subQ16=sQuery(id+"F12.wireOp",EDGE,"E74.1");var subQ18=sQuery(id+"F12.wireOp",EDGE,"E74.8");Q0=qUnion([makeQuery(id+"F12.imprint","IMPRINT",FACE,{"disambiguationData":[TD([[makeQuery(id+"F12.imprint","IMPRINT",EDGE,{"derivedFrom":subQ7}),1.0]])]}),makeQuery(id+"F12.imprint","IMPRINT",FACE,{"disambiguationData":[TD([[makeQuery(id+"F12.imprint","IMPRINT",EDGE,{"derivedFrom":subQ14}),1.0]])]}),makeQuery(id+"F12.imprint","IMPRINT",FACE,{"disambiguationData":[TD([[makeQuery(id+"F12.imprint","IMPRINT",EDGE,{"derivedFrom":subQ16}),1.0]])]}),makeQuery(id+"F12.imprint","IMPRINT",FACE,{"disambiguationData":[TD([[makeQuery(id+"F12.imprint","IMPRINT",EDGE,{"derivedFrom":subQ18}),-1.0]])]})]);}
            var Q1;
            Q1=makeQuery(id+"F5.boolean.opBoolean","SPLIT",FACE,{"disambiguationData":[TD([makeQuery(id+"F5.opExtrude","SWEPT_FACE",FACE,{"disambiguationData":[OSD([sQuery(id+"F4.wireOp",EDGE,"E41")])]})])],"derivedFrom":makeQuery(id+"F3.boolean.opBoolean","COPY",FACE,{"derivedFrom":makeQuery(id+"F3.opExtrude","CAP_FACE",FACE,{"disambiguationData":[OSD([sQuery(id+"F0.wireOp",EDGE,"E25.0"),sQuery(id+"F0.wireOp",EDGE,"E25.1"),sQuery(id+"F0.wireOp",EDGE,"E25.2"),sQuery(id+"F0.wireOp",EDGE,"E25.3"),sQuery(id+"F0.wireOp",EDGE,"E25.4"),sQuery(id+"F0.wireOp",EDGE,"E25.5"),sQuery(id+"F0.wireOp",EDGE,"E25.6"),sQuery(id+"F0.wireOp",EDGE,"E25.7")])],"isStart":false})})});
            extrude(context, id + "F13", {"entities" : qUnion([Q0]), "operationType" : NewBodyOperationType.REMOVE, "endBound" : BoundingType.UP_TO_SURFACE, "endBoundEntityFace" : qUnion([Q1]), "depth" : 25 * mm});
        }
        {
            var Q0;
            Q0=makeQuery(id+"F3.boolean.opBoolean","COPY",EDGE,{"derivedFrom":makeQuery(id+"F3.opExtrude","CAP_EDGE",EDGE,{"disambiguationData":[OSD([sQuery(id+"F0.wireOp",EDGE,"E25.6")])],"isStart":false})});
            var Q1;
            Q1=makeQuery(id+"F8.boolean.opBoolean","INTERSECT",EDGE,{"derivedFrom":[makeQuery(id+"F5.opExtrude","SWEPT_FACE",FACE,{"disambiguationData":[OSD([sQuery(id+"F4.wireOp",EDGE,"E30")])]}),makeQuery(id+"F8.opExtrude","CAP_FACE",FACE,{"disambiguationData":[OSD([sQuery(id+"F7.wireOp",EDGE,"E67")])],"isStart":false})]});
            var Q2;
            Q2=makeQuery(id+"F8.boolean.opBoolean","INTERSECT",EDGE,{"disambiguationData":[OD(1.0)],"derivedFrom":[makeQuery(id+"F5.opExtrude","SWEPT_FACE",FACE,{"disambiguationData":[OSD([sQuery(id+"F4.wireOp",EDGE,"E30")])]}),makeQuery(id+"F8.opExtrude","SWEPT_FACE",FACE,{"disambiguationData":[OSD([sQuery(id+"F7.wireOp",EDGE,"E67")])]})]});
            var Q3;
            {var subQ0=makeQuery(id+"F3.boolean.opBoolean","COPY",FACE,{"derivedFrom":makeQuery(id+"F3.opExtrude","CAP_FACE",FACE,{"disambiguationData":[OSD([sQuery(id+"F0.wireOp",EDGE,"E25.0"),sQuery(id+"F0.wireOp",EDGE,"E25.1"),sQuery(id+"F0.wireOp",EDGE,"E25.2"),sQuery(id+"F0.wireOp",EDGE,"E25.3"),sQuery(id+"F0.wireOp",EDGE,"E25.4"),sQuery(id+"F0.wireOp",EDGE,"E25.5"),sQuery(id+"F0.wireOp",EDGE,"E25.6"),sQuery(id+"F0.wireOp",EDGE,"E25.7")])],"isStart":false})});var subQ1=sQuery(id+"F4.wireOp",EDGE,"E30");Q3=makeQuery(id+"F8.boolean.opBoolean","SPLIT",EDGE,{"disambiguationData":[TD([makeQuery(id+"F5.opExtrude","SWEPT_FACE",FACE,{"disambiguationData":[OSD([sQuery(id+"F4.wireOp",EDGE,"E35.filletArc")])]})])],"derivedFrom":makeQuery(id+"F5.opExtrude","TWEAK_EDGE",EDGE,{"derivedFrom":[subQ0,makeQuery(id+"F4.imprint","IMPRINT",EDGE,{"derivedFrom":subQ1})]})});}
            var Q4;
            {var subQ0=sQuery(id+"F0.wireOp",EDGE,"E25.0");var subQ1=sQuery(id+"F0.wireOp",EDGE,"E25.1");var subQ2=sQuery(id+"F0.wireOp",EDGE,"E25.2");var subQ3=sQuery(id+"F0.wireOp",EDGE,"E25.3");var subQ4=sQuery(id+"F0.wireOp",EDGE,"E25.4");var subQ5=sQuery(id+"F0.wireOp",EDGE,"E25.5");var subQ6=sQuery(id+"F0.wireOp",EDGE,"E25.6");var subQ7=sQuery(id+"F0.wireOp",EDGE,"E25.7");Q4=makeQuery(id+"F8.boolean.opBoolean","INTERSECT",EDGE,{"derivedFrom":[makeQuery(id+"F5.boolean.opBoolean","SPLIT",FACE,{"disambiguationData":[TD([makeQuery(id+"F2.opExtrude","SWEPT_FACE",FACE,{"disambiguationData":[OSD([subQ0])]})])],"derivedFrom":makeQuery(id+"F3.boolean.opBoolean","COPY",FACE,{"derivedFrom":makeQuery(id+"F3.opExtrude","CAP_FACE",FACE,{"disambiguationData":[OSD([subQ0,subQ1,subQ2,subQ3,subQ4,subQ5,subQ6,subQ7])],"isStart":false})})}),makeQuery(id+"F8.opExtrude","SWEPT_FACE",FACE,{"disambiguationData":[OSD([sQuery(id+"F7.wireOp",EDGE,"E67")])]})]});}
            var Q5;
            Q5=makeQuery(id+"F8.boolean.opBoolean","INTERSECT",EDGE,{"disambiguationData":[OD(0.0)],"derivedFrom":[makeQuery(id+"F5.opExtrude","SWEPT_FACE",FACE,{"disambiguationData":[OSD([sQuery(id+"F4.wireOp",EDGE,"E30")])]}),makeQuery(id+"F8.opExtrude","SWEPT_FACE",FACE,{"disambiguationData":[OSD([sQuery(id+"F7.wireOp",EDGE,"E67")])]})]});
            fillet(context, id + "F14", {"entities" : qUnion([Q0, Q1, Q2, Q3, Q4, Q5]), "radius" : 3 * mm, "tangentPropagation" : true, "allowEdgeOverflow" : false});
        }
        {
            var Q0;
            Q0=makeQuery(id+"F1.opExtrude","CAP_EDGE",EDGE,{"disambiguationData":[OSD([sQuery(id+"F0.wireOp",EDGE,"E1.bottom")])],"isStart":false});
            fillet(context, id + "F15", {"entities" : qUnion([Q0]), "radius" : 2 * mm, "tangentPropagation" : true, "allowEdgeOverflow" : false});
        }
        {
            var Q0;
            Q0=qCreatedBy(makeId("Top.planeOp"),FACE);
            var sketch = newSketch(context, id + "F16", { "sketchPlane" : qUnion([Q0])});
            skLineSegment(sketch, "E79.0", {"start": v(-80, 80) * mm, "end": v(80, 80) * mm});
            skArc(sketch, "E79.1", {"start": v(-80, 80) * mm, "mid": v(-87.07, 77.07) * mm, "end": v(-90, 70) * mm});
            skLineSegment(sketch, "E79.2", {"start": v(-90, -70) * mm, "end": v(-90, 70) * mm});
            skCircle(sketch, "E79.3", {"center": v(-60, 53.33) * mm, "radius": 4 * mm});
            skCircle(sketch, "E79.4", {"center": v(60, 53.33) * mm, "radius": 4 * mm});
            skArc(sketch, "E79.5", {"start": v(90, 70) * mm, "mid": v(87.07, 77.07) * mm, "end": v(80, 80) * mm});
            skLineSegment(sketch, "E79.6", {"start": v(90, -70) * mm, "end": v(90, 70) * mm});
            skCircle(sketch, "E79.7", {"center": v(60, -53.33) * mm, "radius": 4 * mm});
            skArc(sketch, "E79.8", {"start": v(80, -80) * mm, "mid": v(87.07, -77.07) * mm, "end": v(90, -70) * mm});
            skLineSegment(sketch, "E79.9", {"start": v(-80, -80) * mm, "end": v(80, -80) * mm});
            skArc(sketch, "E79.10", {"start": v(-90, -70) * mm, "mid": v(-87.07, -77.07) * mm, "end": v(-80, -80) * mm});
            skCircle(sketch, "E79.11", {"center": v(-60, -53.33) * mm, "radius": 4 * mm});
            skArc(sketch, "E79.12", {"start": v(-52.38, -47.01) * mm, "mid": v(0, -53.33) * mm, "end": v(52.38, -47.01) * mm});
            skArc(sketch, "E79.13", {"start": v(-60, -37.3) * mm, "mid": v(-57.87, -43.47) * mm, "end": v(-52.38, -47.01) * mm});
            skLineSegment(sketch, "E79.14", {"start": v(-60, 37.3) * mm, "end": v(-60, -37.3) * mm});
            skArc(sketch, "E79.15", {"start": v(-52.38, 47.01) * mm, "mid": v(-57.87, 43.47) * mm, "end": v(-60, 37.3) * mm});
            skArc(sketch, "E79.16", {"start": v(52.38, 47.01) * mm, "mid": v(0, 53.33) * mm, "end": v(-52.38, 47.01) * mm});
            skArc(sketch, "E79.17", {"start": v(60, 37.3) * mm, "mid": v(57.87, 43.47) * mm, "end": v(52.38, 47.01) * mm});
            skLineSegment(sketch, "E79.18", {"start": v(60, 37.3) * mm, "end": v(60, -37.3) * mm});
            skArc(sketch, "E79.19", {"start": v(52.38, -47.01) * mm, "mid": v(57.87, -43.47) * mm, "end": v(60, -37.3) * mm});
            skLineSegment(sketch, "E80", {"start": v(0, 80) * mm, "end": v(0, 110) * mm, "construction": true});
            skCircle(sketch, "E81", {"center": v(0, 110) * mm, "radius": 6 * mm});
            skLineSegment(sketch, "E82", {"start": v(-32.73, 80) * mm, "end": v(-14.73, 98) * mm});
            skLineSegment(sketch, "E83", {"start": v(-14.73, 98) * mm, "end": v(-14.73, 110) * mm});
            skLineSegment(sketch, "E84", {"start": v(33.27, 80) * mm, "end": v(15.27, 98) * mm});
            skLineSegment(sketch, "E85", {"start": v(15.27, 98) * mm, "end": v(15.27, 110) * mm});
            skArc(sketch, "E86", {"start": v(15.27, 110) * mm, "mid": v(0.27, 125) * mm, "end": v(-14.73, 110) * mm});
            skLineSegment(sketch, "E87", {"start": v(-90, 0) * mm, "end": v(90, 0) * mm, "construction": true});
            skLineSegment(sketch, "E88.MirrorCS", {"start": v(-32.73, -80) * mm, "end": v(-14.73, -98) * mm});
            skLineSegment(sketch, "E89.MirrorCS", {"start": v(-14.73, -98) * mm, "end": v(-14.73, -110) * mm});
            skArc(sketch, "E90.MirrorCS", {"start": v(15.27, -110) * mm, "mid": v(0.27, -125) * mm, "end": v(-14.73, -110) * mm});
            skLineSegment(sketch, "E91.MirrorCS", {"start": v(15.27, -98) * mm, "end": v(15.27, -110) * mm});
            skLineSegment(sketch, "E92.MirrorCS", {"start": v(33.27, -80) * mm, "end": v(15.27, -98) * mm});
            skArc(sketch, "E93.MirrorCS", {"start": v(-80, -80) * mm, "mid": v(-87.07, -77.07) * mm, "end": v(-90, -70) * mm});
            skLineSegment(sketch, "E94.MirrorCS", {"start": v(0, -80) * mm, "end": v(0, -110) * mm, "construction": true});
            skCircle(sketch, "E95.MirrorC", {"center": v(0, -110) * mm, "radius": 6 * mm});
            skSolve(sketch);
        }
        {
            var Q0;
            Q0=makeQuery(id+"F16.imprint","IMPRINT",FACE,{"disambiguationData":[TD([[makeQuery(id+"F16.imprint","IMPRINT",EDGE,{"derivedFrom":sQuery(id+"F16.wireOp",EDGE,"E81")}),-1.0]])]});
            var Q1;
            {var subQ5=sQuery(id+"F16.wireOp",EDGE,"E79.1");Q1=makeQuery(id+"F16.imprint","IMPRINT",FACE,{"disambiguationData":[TD([[makeQuery(id+"F16.imprint","IMPRINT",EDGE,{"derivedFrom":subQ5}),1.0]])]});}
            var Q2;
            {var subQ1=sQuery(id+"F16.wireOp",EDGE,"E88.MirrorCS");Q2=makeQuery(id+"F16.imprint","IMPRINT",FACE,{"disambiguationData":[TD([[makeQuery(id+"F16.imprint","IMPRINT",EDGE,{"derivedFrom":subQ1}),1.0]])]});}
            extrude(context, id + "F17", {"entities" : qUnion([Q0, Q1, Q2]), "operationType" : NewBodyOperationType.ADD, "endBound" : BoundingType.SYMMETRIC, "depth" : 6 * mm});
        }
    });
